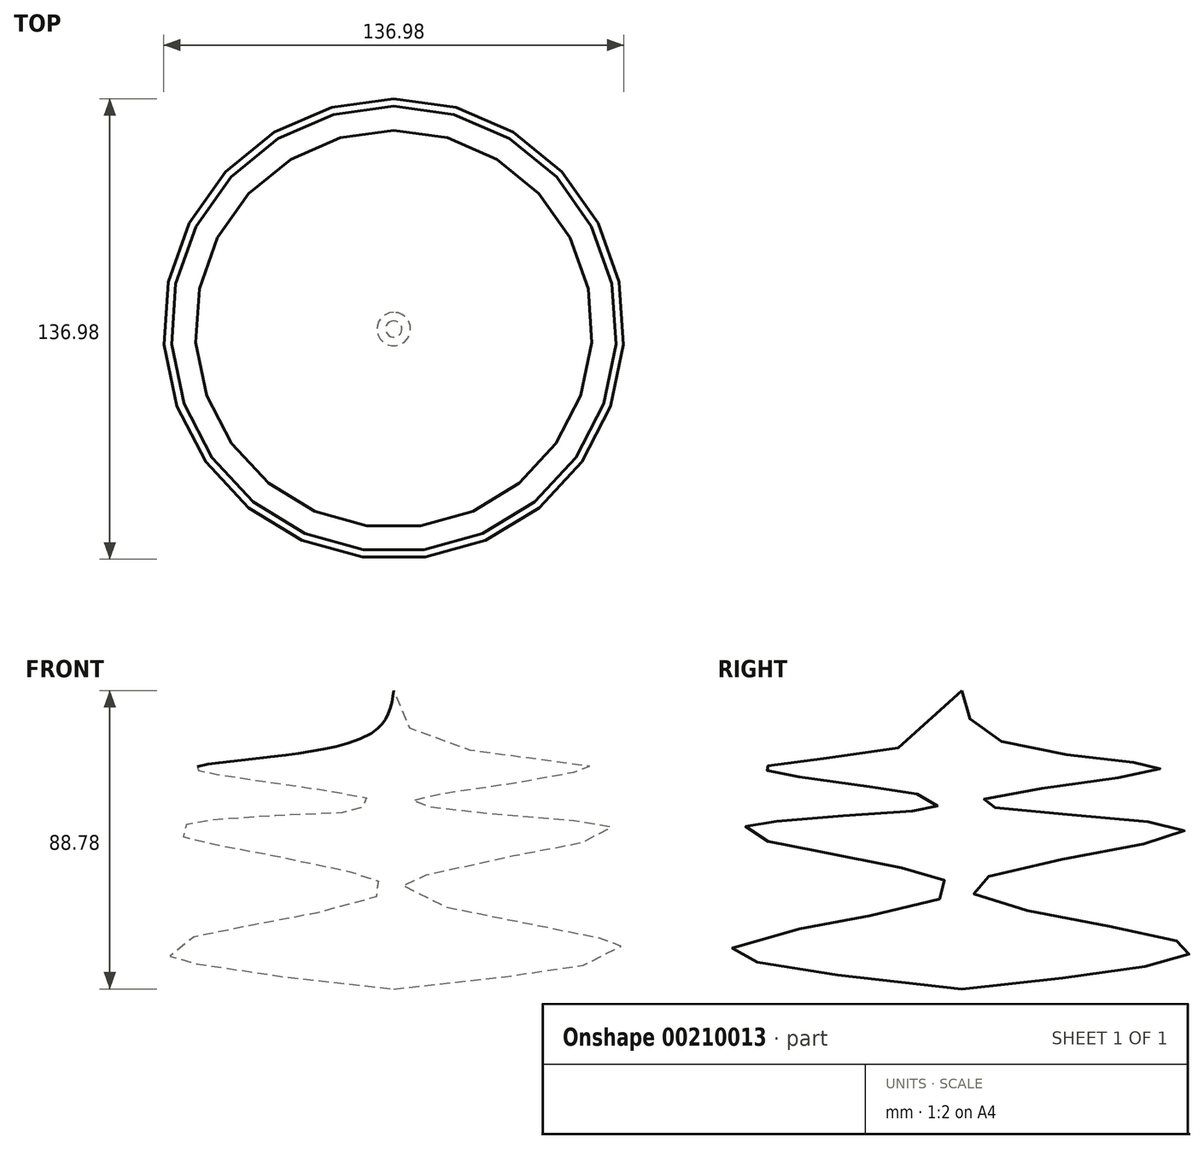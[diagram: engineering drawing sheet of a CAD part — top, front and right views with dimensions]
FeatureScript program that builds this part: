
annotation { "Feature Type Name" : "Feature", "Feature Type Description" : "" }
export const myFeature = defineFeature(function(context is Context, id is Id, definition is map)
    precondition{}
    {
        {
            var Q0;
            Q0=qCreatedBy(makeId("Right.planeOp"),FACE);
            var sketch = newSketch(context, id + "F0", { "sketchPlane" : qUnion([Q0])});
            skFitSpline(sketch, "E0", {"points": [v(0, 65.49) * mm, v(10.63, 50.8) * mm, v(58.77, 42.04) * mm, v(5, 32.04) * mm, v(66.27, 23.91) * mm, v(2.5, 7.03) * mm, v(66.9, -10.16) * mm, v(0, -23.29) * mm], "startDerivative": vector(27.94, -199.94) * mm, "endDerivative": vector(-712.92, -75.18) * mm});
            skLineSegment(sketch, "E1", {"start": v(0, 74.03) * mm, "end": v(0, 68.55) * mm});
            skSolve(sketch);
        }
        {
            var Q0;
            Q0=sQuery(id+"F0.wireOp",EDGE,"E0");
            var Q1;
            Q1=sQuery(id+"F0.wireOp",EDGE,"E1");
            revolve(context, id + "F1", {"bodyType" : ToolBodyType.SURFACE, "surfaceEntities" : qUnion([Q0]), "axis" : qUnion([Q1]), "revolveType" : RevolveType.FULL});
        }
    });
